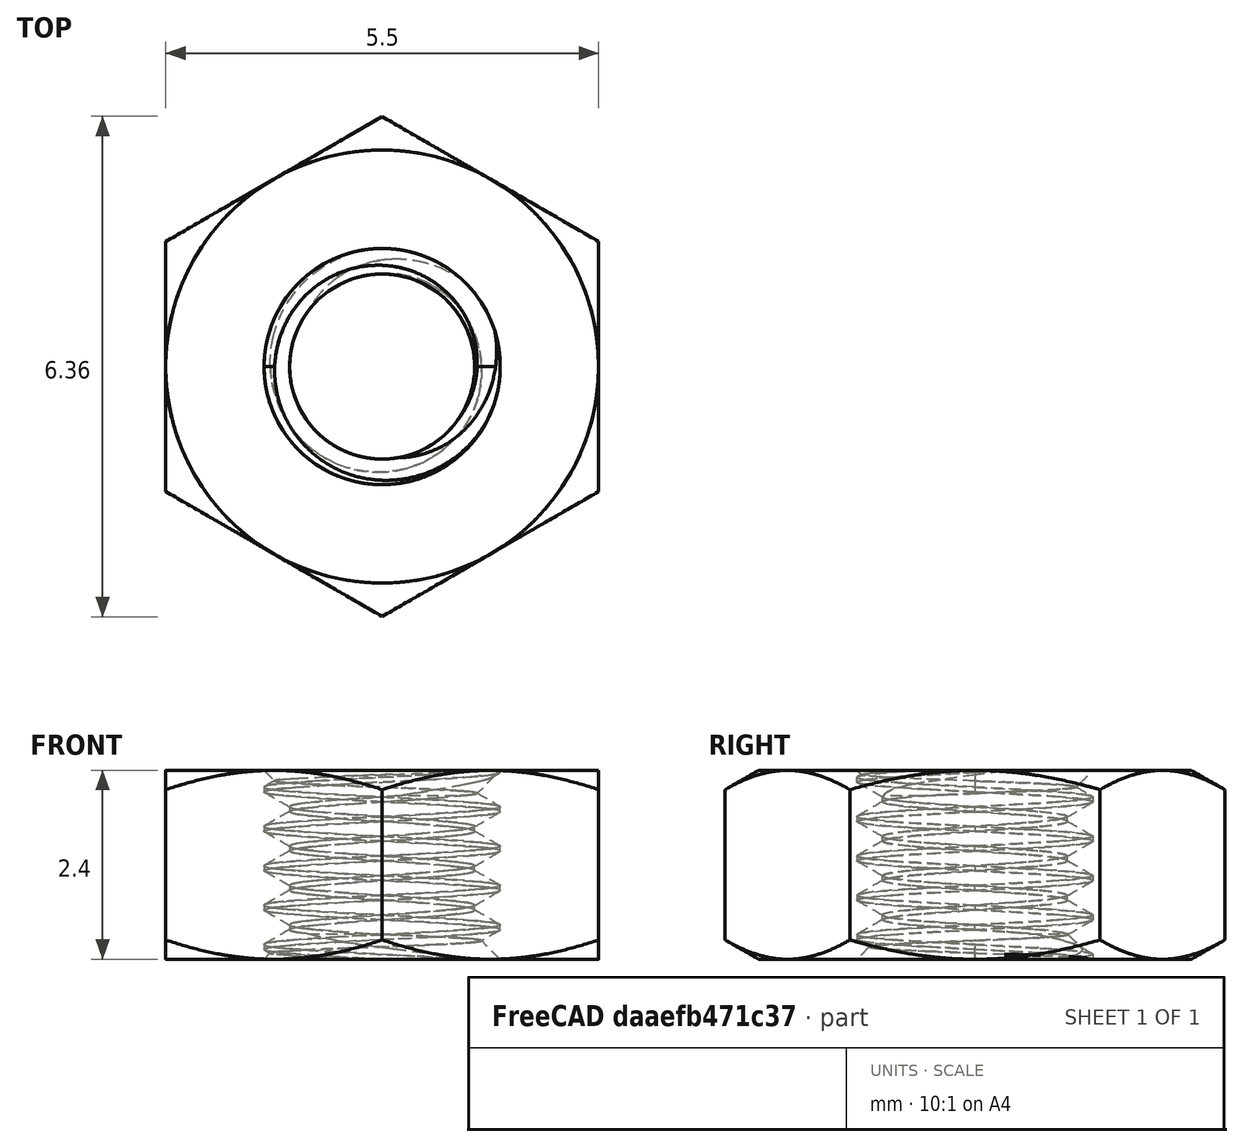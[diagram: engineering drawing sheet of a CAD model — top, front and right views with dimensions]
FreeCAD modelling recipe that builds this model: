
FCSTD DOCUMENT  (FreeCAD 0.19R)
Label: Hex_Nut_M3
License: All rights reserved
LicenseURL: http://en.wikipedia.org/wiki/All_rights_reserved
objects: PartDesign::CoordinateSystem×2, Part::Feature×1, PartDesign::FeatureBase×1, PartDesign::Body×1
note: 5 computed .brp shape members not serialized (recipe doc carries the construction recipe); baked Part::Feature solids carry a one-line shape summary decoded from their .brp

FEATURE [Part::Feature] _1828A211_18_8_Stainless_Steel_Hex_Nut
  shape: bbox 6.351 x 6.351 x 2.771 mm, 48 faces, 0 solids (baked)
FEATURE [PartDesign::FeatureBase] BaseFeature
  BaseFeature = -> _1828A211_18_8_Stainless_Steel_Hex_Nut
FEATURE [PartDesign::CoordinateSystem] Local_CS
  AttacherType = Attacher::AttachEngine3D
  MapMode = 11
  Placement = pos=(-4e-16,4e-16,1.2) rot=(-0.258819,0.965926,0;3.14159rad)
  Support = -> [BaseFeature]
FEATURE [PartDesign::CoordinateSystem] Local_CS001
  AttacherType = Attacher::AttachEngine3D
  AttachmentOffset = pos=(0,0,0) rot=(0,0,1;1.5708rad)
  MapMode = 11
  Placement = pos=(7e-16,-4e-16,-1.2) rot=(0,0,1;2.0944rad)
  Support = -> [BaseFeature]
FEATURE [PartDesign::Body] Body
  BaseFeature = -> _1828A211_18_8_Stainless_Steel_Hex_Nut
  Group = -> [BaseFeature,Local_CS,Local_CS001]
  Origin = -> Origin
  Tip = -> BaseFeature
